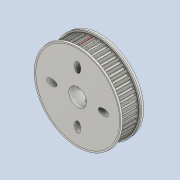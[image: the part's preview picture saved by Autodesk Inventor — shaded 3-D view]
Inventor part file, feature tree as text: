
AUTODESK INVENTOR PART (.ipt)
format: ipt  version: 2020 (Build 240168000, 168)  size: 815,616 bytes
history: native  units: mm (DEFAULTED — no unit token found)
features: other x6, extrude x4, sketch x4, pattern_circular x2, hole x2, fillet x1, plane x1, reference x1, projected_geometry x1
ambient origin geometry x8: Origin, YZ Plane, XZ Plane, XY Plane, X Axis, Y Axis, Z Axis, Center Point
bodies: Solid1 (feature_tree)
feature tree (22):
  other  "Pulley Sketch"
  extrude  "Base Body"  Depth=0.3mm
  extrude  "Tooth"  Depth=8.726646mm
  fillet  "Tooth Fillet"  Radius=1.05mm
  pattern_circular  "Teeth"  [2 undecoded]
  other  "Left flange"
  other  "Right flange"
  hole  "Hole1"  [1 undecoded]
  extrude  "Extrusion3"  Depth=1.0mm
  plane  "Work Plane3"
  hole  "Hole2"  [1 undecoded]
  pattern_circular  "Circular Pattern2"  Count=20  [1 undecoded]
  extrude  "Extrusion5"  TaperAngle=360.0deg  [1 undecoded]
  sketch  "Sketch2"  dims[d0=15.915494mm d1=0.3mm]
  sketch  "Sketch3"  dims[d2=0.75mm d3=8.726646mm d4=1.05mm]
  reference  "Reference1"
  sketch  "Sketch9"  dims[d5=8.0mm]
  sketch  "Sketch10"  dims[d6=0.0mm d7=8.0mm d8=0.0mm d9=0.2mm d10=0.3mm d11=200.0mm d12=360.0deg d15=0.0mm d16=0.0mm d17=8.3mm d18=6.0mm d19=3.023mm d20=2.0mm d21=14.3117mm d22=8.0mm d23=0.0mm d24=11.0mm d25=2.0mm d26=0.0mm d32=3.0mm d33=2.8mm d34=6.0mm d35=3.023mm d36=2.0mm d37=14.3117mm d38=15.0mm d39=0.0mm d40=40.0mm d41=360.0deg d43=1.0mm d44=0.0mm]
  projected_geometry  "Projected Loop1"
  parser-record x1  (decoder bookkeeping rows leaked as tree rows — omitted from the tree; the rows remain in map.json)
  other  "10-03-00 AnsambluZ_V2.iam"
  other  "ISO 1224-1 (Metric) 18 - 8 x 16 x 4:1"
note: 6 required parameter values undecoded (feature->parameter linkage not recoverable at this tier; creation-order binding heuristic only, values carry confidence <= 0.55)
note: 1 file-system path scrubbed to <path> (originals preserved in map.json)
